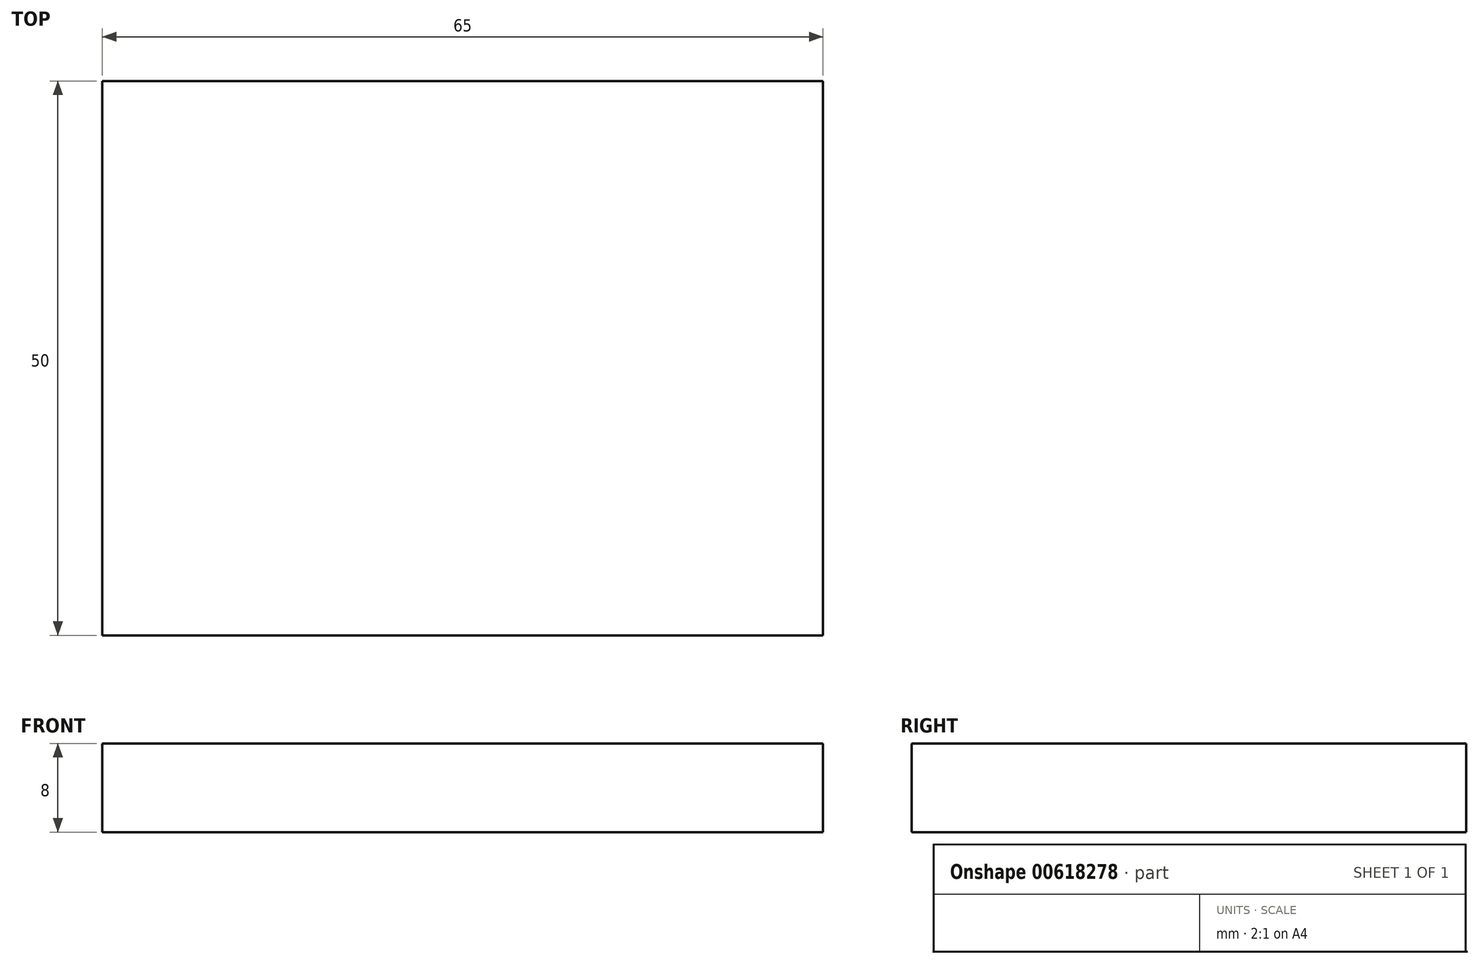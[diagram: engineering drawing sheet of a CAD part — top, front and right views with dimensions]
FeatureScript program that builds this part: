
annotation { "Feature Type Name" : "Feature", "Feature Type Description" : "" }
export const myFeature = defineFeature(function(context is Context, id is Id, definition is map)
    precondition{}
    {
        {
            var Q0;
            Q0=qCreatedBy(makeId("Top.planeOp"),FACE);
            var sketch = newSketch(context, id + "F0", { "sketchPlane" : qUnion([Q0])});
            skLineSegment(sketch, "E0.bottom", {"start": v(32.5, 25) * mm, "end": v(-32.5, 25) * mm});
            skLineSegment(sketch, "E0.top", {"start": v(32.5, -25) * mm, "end": v(-32.5, -25) * mm});
            skLineSegment(sketch, "E0.left", {"start": v(32.5, 25) * mm, "end": v(32.5, -25) * mm});
            skLineSegment(sketch, "E0.right", {"start": v(-32.5, 25) * mm, "end": v(-32.5, -25) * mm});
            skPoint(sketch, "E0.middle", {"position": v(0, 0) * mm});
            skCircle(sketch, "E1", {"center": v(-15, 10) * mm, "radius": 2.5 * mm});
            skCircle(sketch, "E2", {"center": v(-2.5, 10) * mm, "radius": 5 * mm});
            skCircle(sketch, "E3", {"center": v(17.5, 10) * mm, "radius": 10 * mm});
            skLineSegment(sketch, "E4.bottom", {"start": v(20, -7.5) * mm, "end": v(15, -7.5) * mm});
            skLineSegment(sketch, "E4.top", {"start": v(20, -12.5) * mm, "end": v(15, -12.5) * mm});
            skLineSegment(sketch, "E4.left", {"start": v(20, -7.5) * mm, "end": v(20, -12.5) * mm});
            skLineSegment(sketch, "E4.right", {"start": v(15, -7.5) * mm, "end": v(15, -12.5) * mm});
            skPoint(sketch, "E4.middle", {"position": v(17.5, -10) * mm});
            skLineSegment(sketch, "E5.bottom", {"start": v(10, -5) * mm, "end": v(0, -5) * mm});
            skLineSegment(sketch, "E5.top", {"start": v(10, -15) * mm, "end": v(0, -15) * mm});
            skLineSegment(sketch, "E5.left", {"start": v(10, -5) * mm, "end": v(10, -15) * mm});
            skLineSegment(sketch, "E5.right", {"start": v(0, -5) * mm, "end": v(0, -15) * mm});
            skPoint(sketch, "E5.middle", {"position": v(5, -10) * mm});
            skLineSegment(sketch, "E6.bottom", {"start": v(-5, 0) * mm, "end": v(-25, 0) * mm});
            skLineSegment(sketch, "E6.top", {"start": v(-5, -20) * mm, "end": v(-25, -20) * mm});
            skLineSegment(sketch, "E6.left", {"start": v(-5, 0) * mm, "end": v(-5, -20) * mm});
            skLineSegment(sketch, "E6.right", {"start": v(-25, 0) * mm, "end": v(-25, -20) * mm});
            skPoint(sketch, "E6.middle", {"position": v(-15, -10) * mm});
            skSolve(sketch);
        }
        {
            var Q0;
            Q0 = qSketchRegion(id + "F0", true);
            extrude(context, id + "F1", {"entities" : qUnion([Q0]), "depth" : 5 * mm, "offsetDistance" : 25 * mm});
        }
        {
            var Q0;
            Q0=makeQuery(id+"F0.imprint","IMPRINT",FACE,{"disambiguationData":[TD([[makeQuery(id+"F0.imprint","IMPRINT",EDGE,{"derivedFrom":sQuery(id+"F0.wireOp",EDGE,"E6.bottom")}),1.0]])]});
            var Q1;
            Q1=makeQuery(id+"F0.imprint","IMPRINT",FACE,{"disambiguationData":[TD([[makeQuery(id+"F0.imprint","IMPRINT",EDGE,{"derivedFrom":sQuery(id+"F0.wireOp",EDGE,"E5.bottom")}),1.0]])]});
            var Q2;
            Q2=makeQuery(id+"F0.imprint","IMPRINT",FACE,{"disambiguationData":[TD([[makeQuery(id+"F0.imprint","IMPRINT",EDGE,{"derivedFrom":sQuery(id+"F0.wireOp",EDGE,"E4.bottom")}),1.0]])]});
            var Q3;
            Q3=makeQuery(id+"F0.imprint","IMPRINT",FACE,{"disambiguationData":[TD([[makeQuery(id+"F0.imprint","IMPRINT",EDGE,{"derivedFrom":sQuery(id+"F0.wireOp",EDGE,"E3")}),1.0]])]});
            var Q4;
            Q4=makeQuery(id+"F0.imprint","IMPRINT",FACE,{"disambiguationData":[TD([[makeQuery(id+"F0.imprint","IMPRINT",EDGE,{"derivedFrom":sQuery(id+"F0.wireOp",EDGE,"E2")}),1.0]])]});
            var Q5;
            Q5=makeQuery(id+"F0.imprint","IMPRINT",FACE,{"disambiguationData":[TD([[makeQuery(id+"F0.imprint","IMPRINT",EDGE,{"derivedFrom":sQuery(id+"F0.wireOp",EDGE,"E1")}),1.0]])]});
            extrude(context, id + "F2", {"entities" : qUnion([Q0, Q1, Q2, Q3, Q4, Q5]), "depth" : 5 * mm, "offsetDistance" : 25 * mm});
        }
        {
            var Q0;
            Q0=makeQuery(id+"F0.imprint","IMPRINT",FACE,{"disambiguationData":[TD([[makeQuery(id+"F0.imprint","IMPRINT",EDGE,{"derivedFrom":sQuery(id+"F0.wireOp",EDGE,"E0.bottom")}),1.0]])]});
            var Q1;
            Q1=makeQuery(id+"F0.imprint","IMPRINT",FACE,{"disambiguationData":[TD([[makeQuery(id+"F0.imprint","IMPRINT",EDGE,{"derivedFrom":sQuery(id+"F0.wireOp",EDGE,"E6.bottom")}),1.0]])]});
            var Q2;
            Q2=makeQuery(id+"F0.imprint","IMPRINT",FACE,{"disambiguationData":[TD([[makeQuery(id+"F0.imprint","IMPRINT",EDGE,{"derivedFrom":sQuery(id+"F0.wireOp",EDGE,"E1")}),1.0]])]});
            var Q3;
            Q3=makeQuery(id+"F0.imprint","IMPRINT",FACE,{"disambiguationData":[TD([[makeQuery(id+"F0.imprint","IMPRINT",EDGE,{"derivedFrom":sQuery(id+"F0.wireOp",EDGE,"E2")}),1.0]])]});
            var Q4;
            Q4=makeQuery(id+"F0.imprint","IMPRINT",FACE,{"disambiguationData":[TD([[makeQuery(id+"F0.imprint","IMPRINT",EDGE,{"derivedFrom":sQuery(id+"F0.wireOp",EDGE,"E5.bottom")}),1.0]])]});
            var Q5;
            Q5=makeQuery(id+"F0.imprint","IMPRINT",FACE,{"disambiguationData":[TD([[makeQuery(id+"F0.imprint","IMPRINT",EDGE,{"derivedFrom":sQuery(id+"F0.wireOp",EDGE,"E4.bottom")}),1.0]])]});
            var Q6;
            Q6=makeQuery(id+"F0.imprint","IMPRINT",FACE,{"disambiguationData":[TD([[makeQuery(id+"F0.imprint","IMPRINT",EDGE,{"derivedFrom":sQuery(id+"F0.wireOp",EDGE,"E3")}),1.0]])]});
            extrude(context, id + "F3", {"entities" : qUnion([Q0, Q1, Q2, Q3, Q4, Q5, Q6]), "operationType" : NewBodyOperationType.ADD, "oppositeDirection" : true, "depth" : 3 * mm, "offsetDistance" : 25 * mm});
        }
    });
